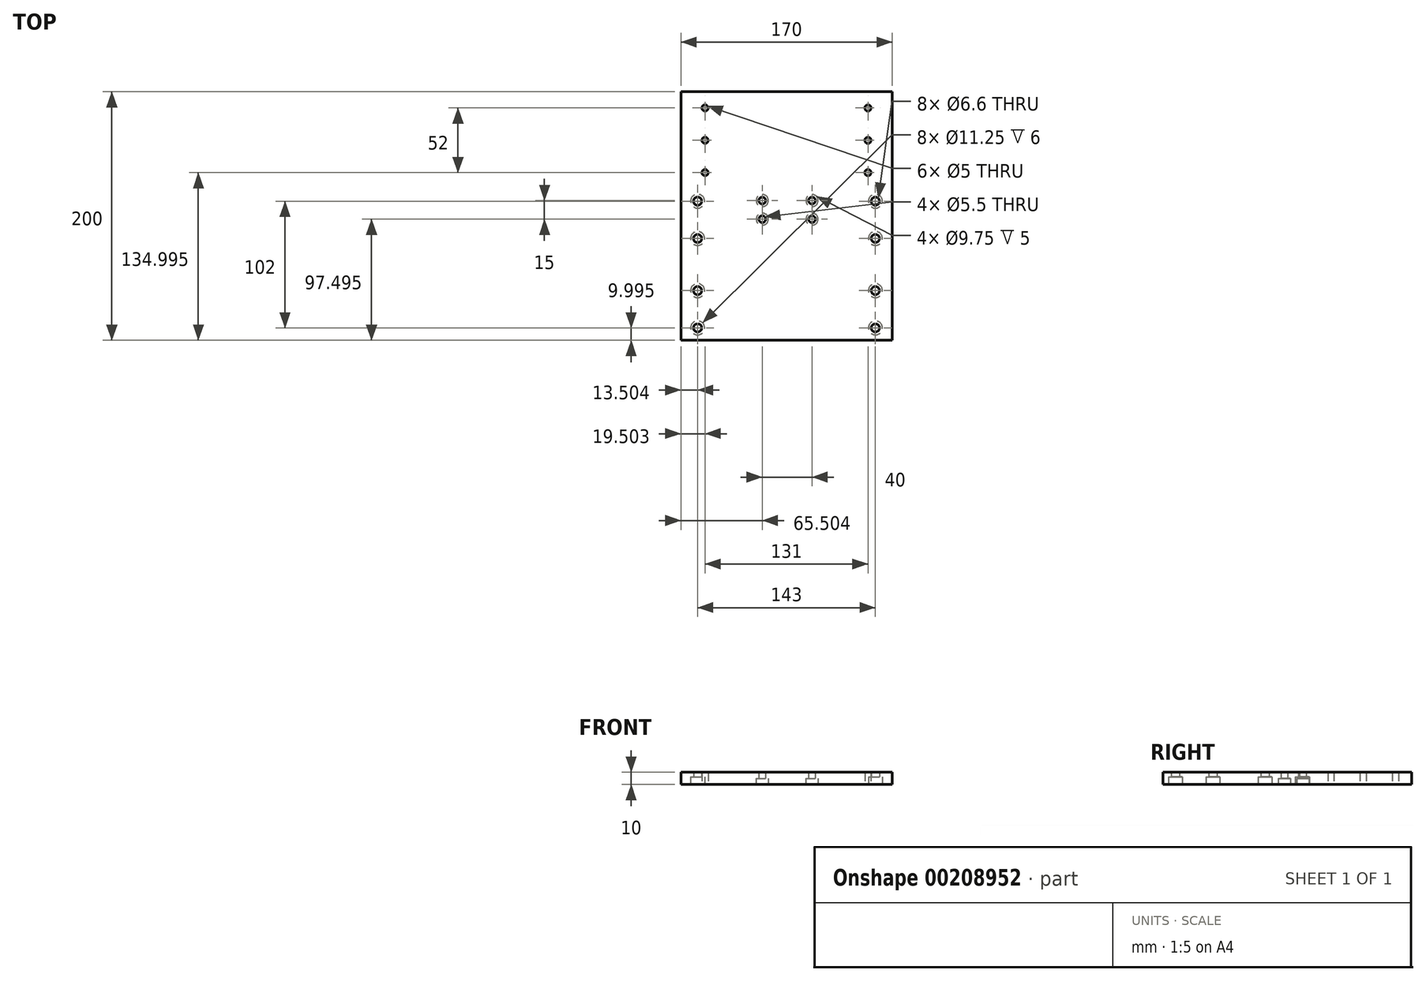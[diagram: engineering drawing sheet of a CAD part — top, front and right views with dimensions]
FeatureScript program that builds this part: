
annotation { "Feature Type Name" : "Feature", "Feature Type Description" : "" }
export const myFeature = defineFeature(function(context is Context, id is Id, definition is map)
    precondition{}
    {
        {
            var Q0;
            Q0=qCreatedBy(makeId("Top.planeOp"),FACE);
            var sketch = newSketch(context, id + "F0", { "sketchPlane" : qUnion([Q0])});
            skLineSegment(sketch, "E0.bottom", {"start": v(-40.6, 153.74) * mm, "end": v(109.4, 153.74) * mm});
            skLineSegment(sketch, "E0.top", {"start": v(-40.6, -46.26) * mm, "end": v(109.4, -46.26) * mm});
            skLineSegment(sketch, "E0.left", {"start": v(-40.6, 153.74) * mm, "end": v(-40.6, -46.26) * mm});
            skLineSegment(sketch, "E0.right", {"start": v(109.4, 153.74) * mm, "end": v(109.4, -46.26) * mm});
            skSolve(sketch);
        }
        {
            var Q0;
            Q0=makeQuery(id+"F0.imprint","IMPRINT",FACE,{"disambiguationData":[TD([[makeQuery(id+"F0.imprint","IMPRINT",EDGE,{"derivedFrom":sQuery(id+"F0.wireOp",EDGE,"E0.bottom")}),-1.0]])]});
            extrude(context, id + "F1", {"entities" : qUnion([Q0]), "depth" : 10 * mm});
        }
        {
            var Q0;
            Q0=makeQuery(id+"F1.opExtrude","CAP_FACE",FACE,{"disambiguationData":[OSD([sQuery(id+"F0.wireOp",EDGE,"E0.bottom"),sQuery(id+"F0.wireOp",EDGE,"E0.top"),sQuery(id+"F0.wireOp",EDGE,"E0.left"),sQuery(id+"F0.wireOp",EDGE,"E0.right")])],"isStart":true});
            var sketch = newSketch(context, id + "F2", { "sketchPlane" : qUnion([Q0])});
            skLineSegment(sketch, "E1", {"start": v(34.4, -153.74) * mm, "end": v(34.4, 46.26) * mm, "construction": true});
            skLineSegment(sketch, "E2", {"start": v(-40.6, -140.74) * mm, "end": v(109.4, -140.74) * mm, "construction": true});
            skLineSegment(sketch, "E3", {"start": v(-40.6, -114.74) * mm, "end": v(109.4, -114.74) * mm, "construction": true});
            skLineSegment(sketch, "E4", {"start": v(-40.6, -88.74) * mm, "end": v(109.4, -88.74) * mm, "construction": true});
            skLineSegment(sketch, "E5", {"start": v(-31.1, -153.74) * mm, "end": v(-31.1, 46.26) * mm, "construction": true});
            skLineSegment(sketch, "E6", {"start": v(99.9, -153.74) * mm, "end": v(99.9, 46.26) * mm, "construction": true});
            skPoint(sketch, "E7", {"position": v(-31.1, -140.74) * mm});
            skPoint(sketch, "E8", {"position": v(-31.1, -114.74) * mm});
            skPoint(sketch, "E9", {"position": v(-31.1, -88.74) * mm});
            skPoint(sketch, "E10", {"position": v(99.9, -140.74) * mm});
            skPoint(sketch, "E11", {"position": v(99.9, -114.74) * mm});
            skPoint(sketch, "E12", {"position": v(99.9, -88.74) * mm});
            skSolve(sketch);
        }
        {
            var Q0;
            Q0=sQuery(id+"F2.wireOp",VERTEX,"E7");
            var Q1;
            Q1=sQuery(id+"F2.wireOp",VERTEX,"E8");
            var Q2;
            Q2=sQuery(id+"F2.wireOp",VERTEX,"E9");
            var Q3;
            Q3=sQuery(id+"F2.wireOp",VERTEX,"E12");
            var Q4;
            Q4=sQuery(id+"F2.wireOp",VERTEX,"E11");
            var Q5;
            Q5=sQuery(id+"F2.wireOp",VERTEX,"E10");
            var Q6;
            Q6=makeQuery(id+"F1.opExtrude","SWEPT_BODY",BODY,{"disambiguationData":[OSD([sQuery(id+"F0.wireOp",EDGE,"E0.bottom"),sQuery(id+"F0.wireOp",EDGE,"E0.top"),sQuery(id+"F0.wireOp",EDGE,"E0.left"),sQuery(id+"F0.wireOp",EDGE,"E0.right")])]});
            hole(context, id + "F3", {"style" : HoleStyle.SIMPLE, "endStyle" : HoleEndStyle.THROUGH, "standardTappedOrClearance" : lookupTablePath({ "standard" : "ISO", "engagement" : "75%", "pitch" : "1 mm", "size" : "M6", "type" : "Tapped" }), "standardBlindInLast" : lookupTablePath({ "standard" : "ISO", "engagement" : "75%", "pitch" : "1 mm", "size" : "M6", "type" : "Tapped" }), "holeDiameter" : 5 * mm, "locations" : qUnion([Q0, Q1, Q2, Q3, Q4, Q5]), "scope" : qUnion([Q6]), "isTappedThrough" : true, "majorDiameter" : 6 * mm, "showTappedDepth" : true});
        }
        {
            var Q0;
            Q0=makeQuery(id+"F1.opExtrude","CAP_FACE",FACE,{"disambiguationData":[OSD([sQuery(id+"F0.wireOp",EDGE,"E0.bottom"),sQuery(id+"F0.wireOp",EDGE,"E0.top"),sQuery(id+"F0.wireOp",EDGE,"E0.left"),sQuery(id+"F0.wireOp",EDGE,"E0.right")])],"isStart":true});
            var sketch = newSketch(context, id + "F4", { "sketchPlane" : qUnion([Q0])});
            skLineSegment(sketch, "E13", {"start": v(109.4, -75.74) * mm, "end": v(-40.6, -75.74) * mm, "construction": true});
            skLineSegment(sketch, "E14", {"start": v(105.9, 46.26) * mm, "end": v(105.9, -153.74) * mm, "construction": true});
            skLineSegment(sketch, "E15", {"start": v(34.4, 46.26) * mm, "end": v(34.4, -153.74) * mm, "construction": true});
            skLineSegment(sketch, "E16.MirrorCS", {"start": v(-37.1, 46.26) * mm, "end": v(-37.1, -153.74) * mm, "construction": true});
            skLineSegment(sketch, "E17", {"start": v(85.9, 46.26) * mm, "end": v(85.9, -153.74) * mm, "construction": true});
            skLineSegment(sketch, "E18.MirrorCS", {"start": v(-17.1, 46.26) * mm, "end": v(-17.1, -153.74) * mm, "construction": true});
            skLineSegment(sketch, "E19", {"start": v(109.4, 31.26) * mm, "end": v(-40.6, 31.26) * mm, "construction": true});
            skLineSegment(sketch, "E20", {"start": v(109.4, 11.26) * mm, "end": v(-40.6, 11.26) * mm, "construction": true});
            skLineSegment(sketch, "E21", {"start": v(109.4, -60.74) * mm, "end": v(-40.6, -60.74) * mm, "construction": true});
            skLineSegment(sketch, "E22", {"start": v(109.4, -40.74) * mm, "end": v(-40.6, -40.74) * mm, "construction": true});
            skPoint(sketch, "E23", {"position": v(85.9, 31.26) * mm});
            skPoint(sketch, "E24", {"position": v(85.9, 11.26) * mm});
            skPoint(sketch, "E25", {"position": v(85.9, -60.74) * mm});
            skPoint(sketch, "E26", {"position": v(85.9, -40.74) * mm});
            skPoint(sketch, "E27", {"position": v(-17.1, 11.26) * mm});
            skPoint(sketch, "E28", {"position": v(-17.1, -40.74) * mm});
            skPoint(sketch, "E29", {"position": v(-17.1, -60.74) * mm});
            skPoint(sketch, "E30", {"position": v(-17.1, 31.26) * mm});
            skPoint(sketch, "E31", {"position": v(105.9, 31.26) * mm});
            skPoint(sketch, "E32", {"position": v(105.9, 11.26) * mm});
            skPoint(sketch, "E33", {"position": v(105.9, -40.74) * mm});
            skPoint(sketch, "E34", {"position": v(105.9, -60.74) * mm});
            skPoint(sketch, "E35", {"position": v(-37.1, 31.26) * mm});
            skPoint(sketch, "E36", {"position": v(-37.1, 11.26) * mm});
            skPoint(sketch, "E37", {"position": v(-37.1, -40.74) * mm});
            skPoint(sketch, "E38", {"position": v(-37.1, -60.74) * mm});
            skLineSegment(sketch, "E39", {"start": v(34.4, 46.26) * mm, "end": v(59.4, 46.26) * mm, "construction": true});
            skLineSegment(sketch, "E40.MirrorCS", {"start": v(34.4, 46.26) * mm, "end": v(9.4, 46.26) * mm, "construction": true});
            skLineSegment(sketch, "E41", {"start": v(59.4, 16.26) * mm, "end": v(34.4, 16.26) * mm, "construction": true});
            skLineSegment(sketch, "E42.MirrorCS", {"start": v(9.4, 16.26) * mm, "end": v(34.4, 16.26) * mm, "construction": true});
            skLineSegment(sketch, "E43", {"start": v(59.4, 46.26) * mm, "end": v(59.4, 16.26) * mm, "construction": true});
            skLineSegment(sketch, "E44", {"start": v(9.4, 46.26) * mm, "end": v(9.4, 16.26) * mm, "construction": true});
            skLineSegment(sketch, "E45", {"start": v(59.4, 31.26) * mm, "end": v(9.4, 31.26) * mm, "construction": true});
            skLineSegment(sketch, "E46", {"start": v(59.4, -51.24) * mm, "end": v(9.4, -51.24) * mm, "construction": true});
            skPoint(sketch, "E47", {"position": v(54.9, -51.24) * mm});
            skPoint(sketch, "E48.MirrorP", {"position": v(13.9, -51.24) * mm});
            skLineSegment(sketch, "E49.bottom", {"start": v(54.9, -51.24) * mm, "end": v(14.9, -51.24) * mm, "construction": true});
            skLineSegment(sketch, "E49.top", {"start": v(54.9, -66.24) * mm, "end": v(14.9, -66.24) * mm, "construction": true});
            skLineSegment(sketch, "E49.left", {"start": v(54.9, -51.24) * mm, "end": v(54.9, -66.24) * mm, "construction": true});
            skLineSegment(sketch, "E49.right", {"start": v(14.9, -51.24) * mm, "end": v(14.9, -66.24) * mm, "construction": true});
            skLineSegment(sketch, "E50", {"start": v(-37.1, 31.26) * mm, "end": v(-37.1, 11.26) * mm, "construction": true});
            skPoint(sketch, "E51", {"position": v(-37.1, 36.26) * mm});
            skPoint(sketch, "E52", {"position": v(-37.1, 6.26) * mm});
            skPoint(sketch, "E53", {"position": v(-37.1, -35.74) * mm});
            skPoint(sketch, "E54", {"position": v(-37.1, -65.74) * mm});
            skPoint(sketch, "E55.MirrorP", {"position": v(105.9, 6.26) * mm});
            skPoint(sketch, "E56.MirrorP", {"position": v(105.9, 36.26) * mm});
            skPoint(sketch, "E57.MirrorP", {"position": v(105.9, -35.74) * mm});
            skPoint(sketch, "E58.MirrorP", {"position": v(105.9, -65.74) * mm});
            skSolve(sketch);
        }
        {
            var Q0;
            Q0=makeQuery(id+"F1.opExtrude","SWEPT_FACE",FACE,{"disambiguationData":[OSD([sQuery(id+"F0.wireOp",EDGE,"E0.right")])]});
            extrude(context, id + "F5", {"entities" : qUnion([Q0]), "operationType" : NewBodyOperationType.ADD, "depth" : 10 * mm});
        }
        {
            var Q0;
            Q0=makeQuery(id+"F1.opExtrude","SWEPT_FACE",FACE,{"disambiguationData":[OSD([sQuery(id+"F0.wireOp",EDGE,"E0.left")])]});
            extrude(context, id + "F6", {"entities" : qUnion([Q0]), "operationType" : NewBodyOperationType.ADD, "depth" : 10 * mm});
        }
        {
            var Q0;
            Q0=sQuery(id+"F4.wireOp",VERTEX,"E51");
            var Q1;
            Q1=sQuery(id+"F4.wireOp",VERTEX,"E52");
            var Q2;
            Q2=sQuery(id+"F4.wireOp",VERTEX,"E56.MirrorP");
            var Q3;
            Q3=sQuery(id+"F4.wireOp",VERTEX,"E55.MirrorP");
            var Q4;
            Q4=sQuery(id+"F4.wireOp",VERTEX,"E57.MirrorP");
            var Q5;
            Q5=sQuery(id+"F4.wireOp",VERTEX,"E58.MirrorP");
            var Q6;
            Q6=sQuery(id+"F4.wireOp",VERTEX,"E54");
            var Q7;
            Q7=sQuery(id+"F4.wireOp",VERTEX,"E53");
            var Q8;
            Q8=makeQuery(id+"F1.opExtrude","SWEPT_BODY",BODY,{"disambiguationData":[OSD([sQuery(id+"F0.wireOp",EDGE,"E0.bottom"),sQuery(id+"F0.wireOp",EDGE,"E0.top"),sQuery(id+"F0.wireOp",EDGE,"E0.left"),sQuery(id+"F0.wireOp",EDGE,"E0.right")])]});
            hole(context, id + "F7", {"style" : HoleStyle.C_BORE, "endStyle" : HoleEndStyle.THROUGH, "standardTappedOrClearance" : lookupTablePath({ "standard" : "ISO", "fit" : "Normal", "size" : "M6", "type" : "Clearance" }), "standardBlindInLast" : lookupTablePath({ "fit" : "Standard", "standard" : "ISO", "size" : "M6", "type" : "Clearance" }), "holeDiameter" : 6.6 * mm, "cBoreDiameter" : 11.25 * mm, "cBoreDepth" : 6 * mm, "locations" : qUnion([Q0, Q1, Q2, Q3, Q4, Q5, Q6, Q7]), "scope" : qUnion([Q8]), "isTappedThrough" : true});
        }
        {
            var Q0;
            Q0=sQuery(id+"F4.wireOp",VERTEX,"E47");
            var Q1;
            Q1=sQuery(id+"F4.wireOp",VERTEX,"bab27757-6492-4608-aa13-f8fd117667d20.MirrorP");
            var Q2;
            Q2=sQuery(id+"F4.wireOp",VERTEX,"ea27ac79-7614-474c-8a79-899a4009a5a80.MirrorP");
            var Q3;
            Q3=sQuery(id+"F4.wireOp",VERTEX,"E49.top.start");
            var Q4;
            Q4=sQuery(id+"F4.wireOp",VERTEX,"E49.bottom.end");
            var Q5;
            Q5=sQuery(id+"F4.wireOp",VERTEX,"E49.top.end");
            var Q6;
            Q6=makeQuery(id+"F1.opExtrude","SWEPT_BODY",BODY,{"disambiguationData":[OSD([sQuery(id+"F0.wireOp",EDGE,"E0.bottom"),sQuery(id+"F0.wireOp",EDGE,"E0.top"),sQuery(id+"F0.wireOp",EDGE,"E0.left"),sQuery(id+"F0.wireOp",EDGE,"E0.right")])]});
            hole(context, id + "F8", {"style" : HoleStyle.C_BORE, "endStyle" : HoleEndStyle.THROUGH, "standardTappedOrClearance" : lookupTablePath({ "standard" : "ISO", "fit" : "Normal", "size" : "M5", "type" : "Clearance" }), "standardBlindInLast" : lookupTablePath({ "fit" : "Standard", "standard" : "ISO", "size" : "M5", "type" : "Clearance" }), "holeDiameter" : 5.5 * mm, "cBoreDiameter" : 9.75 * mm, "cBoreDepth" : 5 * mm, "locations" : qUnion([Q0, Q1, Q2, Q3, Q4, Q5]), "scope" : qUnion([Q6]), "isTappedThrough" : true});
        }
    });
